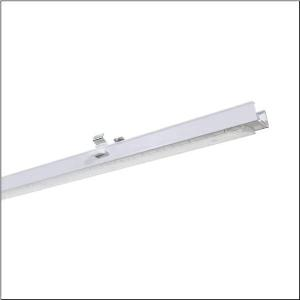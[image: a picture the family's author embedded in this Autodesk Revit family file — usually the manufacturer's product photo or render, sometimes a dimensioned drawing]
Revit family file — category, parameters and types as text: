
# Revit family: trunking_flex_31_51re12mb5cb
name_source: partatom
category: Lighting Fixtures
units: mm (PartAtom-declared; Revit-internal decimal feet)

## family parameters
Cut with Voids When Loaded = No
Host = Face
Light Source = No
Part Type = Normal
Room Calculation Point = No
Round Connector Dimension = Use Diameter
Shared = No

## types (1)
- --- (1 x LED, 11500 lm, 66 W, 5000K)
    Apparent Load = 66 VA
    CIE Flux Codes = 65 91 98 99 100
    Color Rendering = 80
    Color Temperature = 5000K
    Default Elevation = 1800 mm
    Description = Trunking Flex 31, luminaire insert, of extruded aluminium section, coated, traffic white (RAL 9016), length: 1.472mm, width: 91mm, height: 53mm, LED rated luminous flux: 11.500lm, light colour: 850, control gear: ON/OFF Multilumen, with system connector: socket, mains connection: 220..240V, AC, 50/60Hz, rated input power: 66W, luminous flux adjustable on luminaire in eight steps (3450/4380/5800/6700/8350/9200/10500/11500lm ), connected load according to luminous flux setting (19/24/32/37/47/52/60/66W), primary light control with lens, of plastic, primary optical cover: cover, of PMMA, light emission: direct distribution, protection rating (complete): IP20, insulation class (complete): insulation class I (protective earthing), certification: CE, UKCA, impact resistance: IK02, permissible ambient temperature for indoor applications: -20..+40°C, packaging unit: 1 piece
    Height = 58 mm
    Lamp = 1 x LED
    Lamp Light Flux = 11500 lm
    Lamp Power = 66 W
    Lamp count = 1
    Length = 1472 mm
    Luminous efficacy = 174 lm/W
    Manufacturer = Siteco
    ModVariant = No
    Model = 51RE12MB5CB
    Mounting Place = Ceiling
    Mounting Type = Pendant
    Number of Poles = 1
    OnlyDefault = Yes
    Power Factor = 1
    Product Name = Trunking Flex 31
    Product group = luminaire insert
    ProductGroupID = 901
    Protection Class = Protection class I
    Protection Degree = IP 20
    RLX_Detail_Level = 1
    RLX_Emergency_Light_Flux = 0 lm
    RLX_Emergency_Type = 0
    RLX_Emergency_Type_DB = No
    RlxData = <blob elided: 20977 chars, md5=9be0d836>
    Socket = socket
    Standby Power = 0 W
    System Light Flux = 11500 lm
    System Power = 66 W
    Type Comments = factory setting: luminous flux: 100 % | (ON | ON | ON)
    Type Image = l_1266702.jpg
    URL = http://relux.com
    VarID = @adj_027083
    Voltage = 0 V
    Weight = 0.00 kg
    Width = 65 mm

## geometry (parser evidence)
native form markers: Blend x4, Sweep x11
no freeform markers — native parametric forms only
